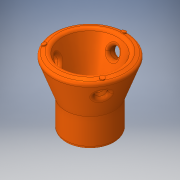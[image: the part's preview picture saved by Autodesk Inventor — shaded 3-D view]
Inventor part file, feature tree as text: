
AUTODESK INVENTOR PART (.ipt)
format: ipt  version: 2016 (Build 200138000, 138)  size: 423,424 bytes
history: native  units: in
note: dims shown in document units (in); Inventor stores cm internally (conversion verified against a paired STEP export)
features: sketch x8, extrude x4, plane x4, fillet x4, pattern_circular x2, revolve x1
ambient origin geometry x8: Origin, YZ Plane, XZ Plane, XY Plane, X Axis, Y Axis, Z Axis, Center Point
bodies: Solid1 (feature_tree)
feature tree (23):
  revolve  "Revolution1"  [1 undecoded]
  extrude  "Extrusion1"  Depth=0.481in
  extrude  "Extrusion2"  TaperAngle=90.0deg  [1 undecoded]
  sketch  "Sketch6"  dims[d6=0.3937in d7=1.0in d8=0.0in d9=0.7874in d10=0.3937in d11=0.0in d12=15.0deg d13=0.3937in]
  plane  "Work Plane1"
  sketch  "Sketch8"  dims[d14=2.3622in d15=0.7874in d16=0.0in d19=1.1811in d20=360.0deg]
  plane  "Work Plane2"
  extrude  "Extrusion3"  Depth=0.3937in TaperAngle=0.0deg
  pattern_circular  "Circular Pattern1"  Count=2  [1 undecoded]
  fillet  "Fillet3"  Radius=0.3937in
  fillet  "Fillet6"  [1 undecoded]
  fillet  "Fillet7"  Radius=0.3937in
  plane  "Work Plane4"
  sketch  "Sketch12"  dims[d25=0.125in]
  plane  "Work Plane5"
  extrude  "Extrusion4"  Depth=0.7874in TaperAngle=0.0deg
  fillet  "Fillet8"  Radius=1.1811in
  pattern_circular  "Circular Pattern2"  [2 undecoded]
  sketch  "Sketch1"  dims[d0=0.9843in d1=1.1811in]
  sketch  "Sketch2"  dims[d2=1.5748in d3=0.481in]
  sketch  "Sketch3"  dims[d4=0.3937in d5=90.0deg]
  sketch  "Sketch9"  dims[d22=0.125in]
  sketch  "Sketch13"  dims[d26=0.125in d27=1.5157in d28=-0.1031in d29=0.1in d30=0.0in d31=0.9in d32=0.125in d33=1.1811in d34=360.0deg]
note: 6 required parameter values undecoded (feature->parameter linkage not recoverable at this tier; creation-order binding heuristic only, values carry confidence <= 0.55)